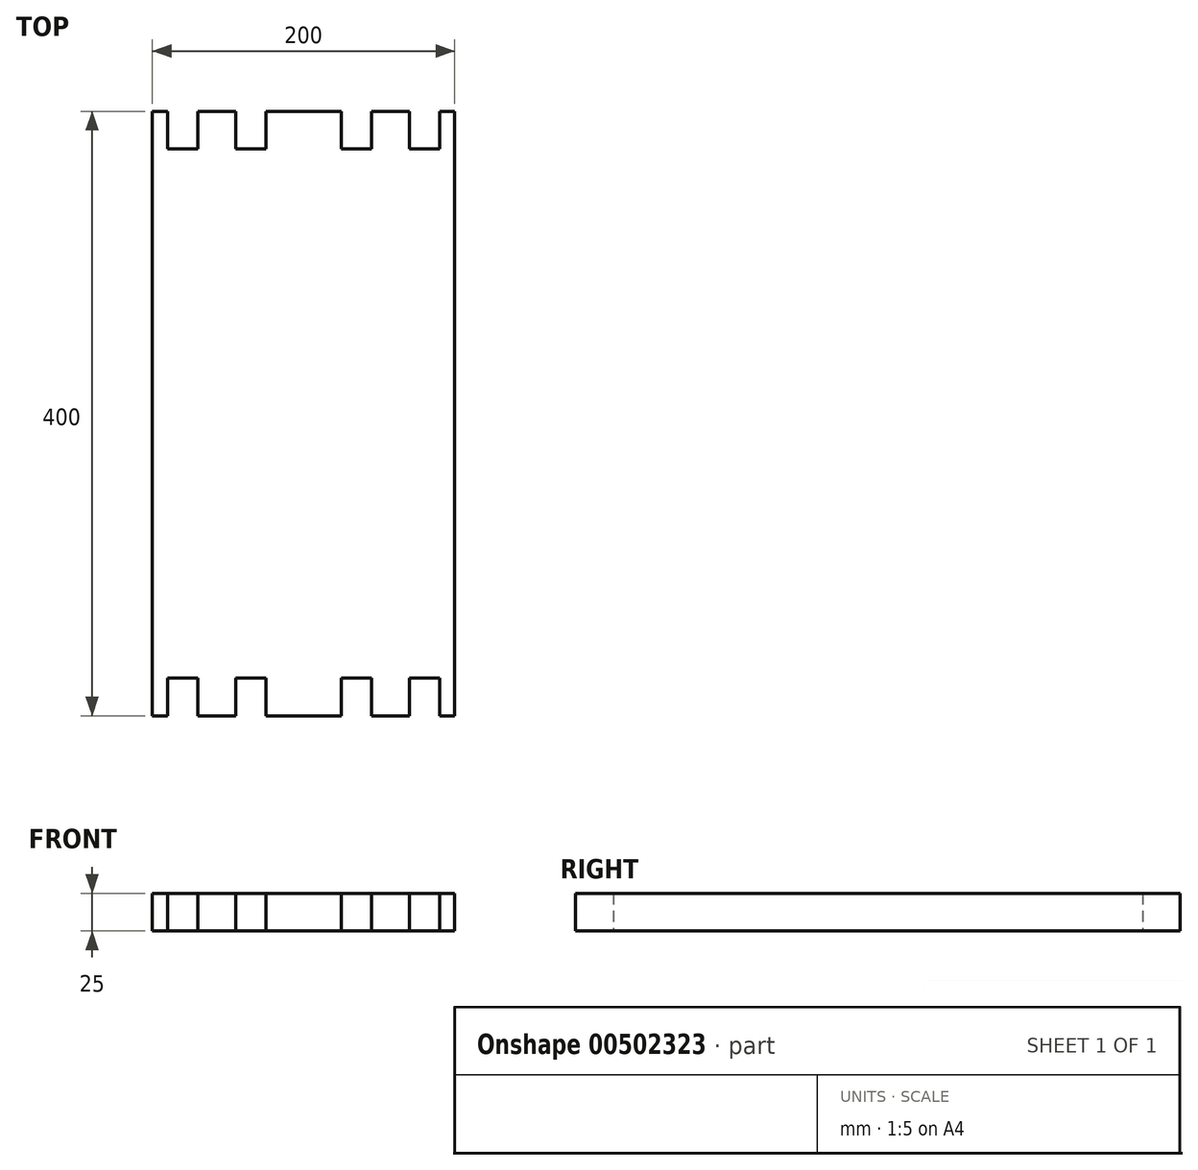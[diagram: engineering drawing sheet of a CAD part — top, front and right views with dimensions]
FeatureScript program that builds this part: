
annotation { "Feature Type Name" : "Feature", "Feature Type Description" : "" }
export const myFeature = defineFeature(function(context is Context, id is Id, definition is map)
    precondition{}
    {
        {
            var Q0;
            Q0=qCreatedBy(makeId("Top.planeOp"),FACE);
            var sketch = newSketch(context, id + "F0", { "sketchPlane" : qUnion([Q0])});
            skLineSegment(sketch, "E0.bottom", {"start": v(100, -200) * mm, "end": v(-100, -200) * mm});
            skLineSegment(sketch, "E0.top", {"start": v(100, 200) * mm, "end": v(-100, 200) * mm});
            skLineSegment(sketch, "E0.left", {"start": v(100, -175) * mm, "end": v(100, 175) * mm});
            skLineSegment(sketch, "E0.right", {"start": v(-100, -175) * mm, "end": v(-100, 175) * mm});
            skPoint(sketch, "E0.middle", {"position": v(0, 0) * mm});
            skLineSegment(sketch, "E1.bottom", {"start": v(-45, 200) * mm, "end": v(-25, 200) * mm});
            skLineSegment(sketch, "E2.bottom", {"start": v(25, 200) * mm, "end": v(45, 200) * mm});
            skLineSegment(sketch, "E3.bottom", {"start": v(70, 200) * mm, "end": v(90, 200) * mm});
            skLineSegment(sketch, "E4.bottom", {"start": v(-70, 200) * mm, "end": v(-90, 200) * mm});
            skLineSegment(sketch, "E5.bottom", {"start": v(-45, -200) * mm, "end": v(-25, -200) * mm});
            skLineSegment(sketch, "E6.bottom", {"start": v(-90, -200) * mm, "end": v(-70, -200) * mm});
            skLineSegment(sketch, "E7.bottom", {"start": v(25, -200) * mm, "end": v(45, -200) * mm});
            skLineSegment(sketch, "E8.bottom", {"start": v(70, -200) * mm, "end": v(90, -200) * mm});
            skPoint(sketch, "E9.trimOffspring.end.orphan", {"position": v(0, -200) * mm});
            skPoint(sketch, "E10.start.orphan", {"position": v(0, 200) * mm});
            skLineSegment(sketch, "E11", {"start": v(-90, 200) * mm, "end": v(-90, 175) * mm});
            skLineSegment(sketch, "E12", {"start": v(-100, 200) * mm, "end": v(-100, 175) * mm});
            skPoint(sketch, "E13.end.orphan", {"position": v(-90, 180) * mm});
            skPoint(sketch, "E13.start.orphan", {"position": v(-100, 180) * mm});
            skLineSegment(sketch, "E14", {"start": v(-70, 200) * mm, "end": v(-70, 175) * mm});
            skLineSegment(sketch, "E15", {"start": v(-45, 200) * mm, "end": v(-45, 175) * mm});
            skLineSegment(sketch, "E16", {"start": v(-25, 200) * mm, "end": v(-25, 175) * mm});
            skLineSegment(sketch, "E17", {"start": v(-25, 175) * mm, "end": v(-26.15, 176.34) * mm});
            skLineSegment(sketch, "E18", {"start": v(25, 200) * mm, "end": v(25, 175) * mm});
            skLineSegment(sketch, "E19", {"start": v(45, 200) * mm, "end": v(45, 175) * mm});
            skLineSegment(sketch, "E20", {"start": v(70, 200) * mm, "end": v(70, 175) * mm});
            skLineSegment(sketch, "E21", {"start": v(90, 200) * mm, "end": v(90, 175) * mm});
            skLineSegment(sketch, "E22", {"start": v(100, 200) * mm, "end": v(100, 175) * mm});
            skLineSegment(sketch, "E23", {"start": v(-100, -200) * mm, "end": v(-100, -175) * mm});
            skLineSegment(sketch, "E24", {"start": v(-90, -200) * mm, "end": v(-90, -175) * mm});
            skLineSegment(sketch, "E25", {"start": v(-70, -200) * mm, "end": v(-70, -175) * mm});
            skLineSegment(sketch, "E26", {"start": v(-45, -200) * mm, "end": v(-45, -175) * mm});
            skLineSegment(sketch, "E27", {"start": v(-25, -200) * mm, "end": v(-25, -175) * mm});
            skLineSegment(sketch, "E28", {"start": v(25, -200) * mm, "end": v(25, -175) * mm});
            skLineSegment(sketch, "E29", {"start": v(45, -200) * mm, "end": v(45, -175) * mm});
            skLineSegment(sketch, "E30", {"start": v(70, -200) * mm, "end": v(70, -175) * mm});
            skLineSegment(sketch, "E31", {"start": v(90, -200) * mm, "end": v(90, -175) * mm});
            skLineSegment(sketch, "E32", {"start": v(90, -175) * mm, "end": v(89.48, -176.7) * mm});
            skLineSegment(sketch, "E33", {"start": v(100, -200) * mm, "end": v(100, -175) * mm});
            skPoint(sketch, "E34.trimOffspring.end.orphan", {"position": v(-45, -180) * mm});
            skPoint(sketch, "E35.end.orphan", {"position": v(-90, -180) * mm});
            skPoint(sketch, "E35.start.orphan", {"position": v(-100, -180) * mm});
            skPoint(sketch, "E36.trimOffspring.start.orphan", {"position": v(45, -180) * mm});
            skLineSegment(sketch, "E37", {"start": v(-90, -175) * mm, "end": v(-70, -175) * mm});
            skLineSegment(sketch, "E38", {"start": v(90, 175) * mm, "end": v(70, 175) * mm});
            skLineSegment(sketch, "E39.trimOffspring", {"start": v(-70, 175) * mm, "end": v(-90, 175) * mm});
            skLineSegment(sketch, "E40.trimOffspring", {"start": v(-25, 175) * mm, "end": v(-45, 175) * mm});
            skLineSegment(sketch, "E41.trimOffspring", {"start": v(45, 175) * mm, "end": v(25, 175) * mm});
            skLineSegment(sketch, "E42.trimOffspring", {"start": v(70, -175) * mm, "end": v(90, -175) * mm});
            skLineSegment(sketch, "E43.trimOffspring", {"start": v(25, -175) * mm, "end": v(45, -175) * mm});
            skLineSegment(sketch, "E44.trimOffspring", {"start": v(-45, -175) * mm, "end": v(-25, -175) * mm});
            skSolve(sketch);
        }
        {
            var Q0;
            Q0=makeQuery(id+"F0.imprint","IMPRINT",FACE,{"disambiguationData":[TD([[makeQuery(id+"F0.imprint","IMPRINT",EDGE,{"derivedFrom":sQuery(id+"F0.wireOp",EDGE,"E0.left")}),1.0]])]});
            extrude(context, id + "F1", {"entities" : qUnion([Q0]), "depth" : 25 * mm, "offsetDistance" : 25 * mm});
        }
    });
